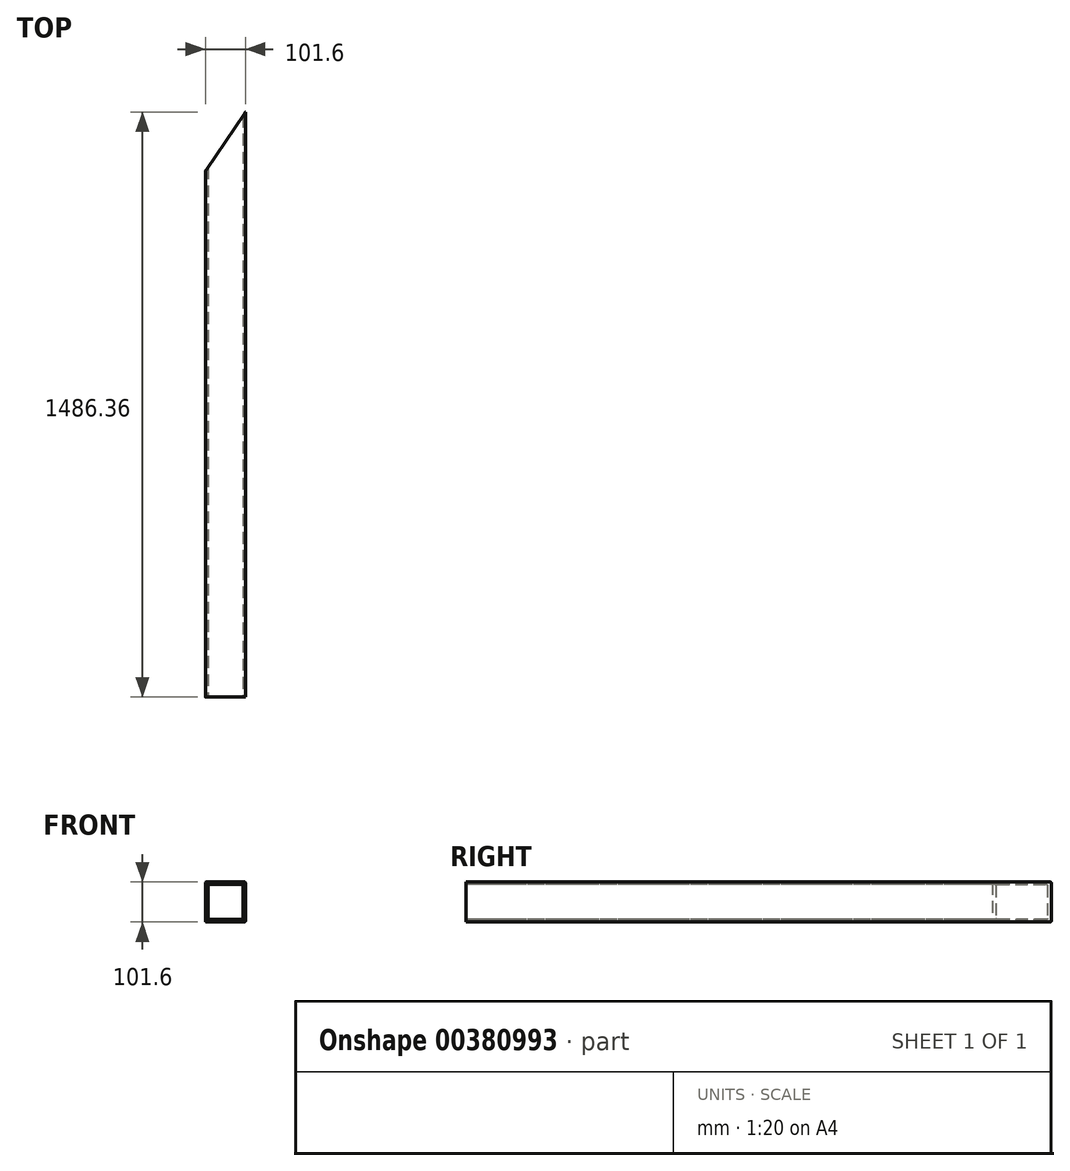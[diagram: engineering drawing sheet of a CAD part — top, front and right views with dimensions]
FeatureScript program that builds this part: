
annotation { "Feature Type Name" : "Feature", "Feature Type Description" : "" }
export const myFeature = defineFeature(function(context is Context, id is Id, definition is map)
    precondition{}
    {
        {
            var Q0;
            Q0=qCreatedBy(makeId("Top.planeOp"),FACE);
            var sketch = newSketch(context, id + "F0", { "sketchPlane" : qUnion([Q0])});
            skLineSegment(sketch, "E0.left", {"start": v(560, 75) * mm, "end": v(560, -75) * mm});
            skPoint(sketch, "E0.middle", {"position": v(0, 0) * mm});
            skLineSegment(sketch, "E1.top", {"start": v(560, -1035) * mm, "end": v(458.4, -1035) * mm});
            skLineSegment(sketch, "E1.left", {"start": v(560, 75) * mm, "end": v(560, -1035) * mm});
            skLineSegment(sketch, "E1.right", {"start": v(458.4, -75) * mm, "end": v(458.4, -1035) * mm});
            skLineSegment(sketch, "E2", {"start": v(458.4, -75) * mm, "end": v(560, 75) * mm});
            skLineSegment(sketch, "E3.left", {"start": v(560, 451.36) * mm, "end": v(560, 301.36) * mm});
            skPoint(sketch, "E3.middle", {"position": v(0, 376.36) * mm});
            skLineSegment(sketch, "E4.top", {"start": v(560, -658.64) * mm, "end": v(458.4, -658.64) * mm});
            skLineSegment(sketch, "E4.left", {"start": v(560, 451.36) * mm, "end": v(560, -658.64) * mm});
            skLineSegment(sketch, "E4.right", {"start": v(458.4, 301.36) * mm, "end": v(458.4, -658.64) * mm});
            skLineSegment(sketch, "E5", {"start": v(458.4, 301.36) * mm, "end": v(560, 451.36) * mm});
            skSolve(sketch);
        }
        {
            var Q0;
            Q0=qSketchRegion(id+"F0",true);
            extrude(context, id + "F1", {"entities" : qUnion([Q0]), "endBound" : BoundingType.SYMMETRIC, "depth" : 101.6 * mm});
        }
        {
            var Q0;
            Q0=makeQuery(id+"F1.opExtrude","SWEPT_FACE",FACE,{"disambiguationData":[OSD([sQuery(id+"F0.wireOp",EDGE,"E1.top")])]});
            var sketch = newSketch(context, id + "F2", { "sketchPlane" : qUnion([Q0])});
            skLineSegment(sketch, "E6.MirrorCS", {"start": v(464.75, -44.45) * mm, "end": v(553.65, -44.45) * mm});
            skLineSegment(sketch, "E7.MirrorCS", {"start": v(464.75, 44.45) * mm, "end": v(464.75, -44.45) * mm});
            skLineSegment(sketch, "E8.MirrorCS", {"start": v(464.75, 44.45) * mm, "end": v(553.65, 44.45) * mm});
            skLineSegment(sketch, "E9.MirrorCS", {"start": v(553.65, 44.45) * mm, "end": v(553.65, -44.45) * mm});
            skSolve(sketch);
        }
        {
            var Q0;
            Q0=makeQuery(id+"F2.imprint","IMPRINT",FACE,{"disambiguationData":[TD([[makeQuery(id+"F2.imprint","IMPRINT",EDGE,{"derivedFrom":sQuery(id+"F2.wireOp",EDGE,"E8.MirrorCS")}),-1.0]])]});
            extrude(context, id + "F3", {"entities" : qUnion([Q0]), "operationType" : NewBodyOperationType.REMOVE, "endBound" : BoundingType.UP_TO_NEXT, "oppositeDirection" : true, "depth" : 25 * mm});
        }
        {
            var Q0;
            Q0=makeQuery(id+"F1.opExtrude","CAP_EDGE",EDGE,{"disambiguationData":[OSD([sQuery(id+"F0.wireOp",EDGE,"E1.left"),sQuery(id+"F0.wireOp",EDGE,"E4.left")])],"isStart":false});
            var Q1;
            Q1=makeQuery(id+"F1.opExtrude","CAP_EDGE",EDGE,{"disambiguationData":[OSD([sQuery(id+"F0.wireOp",EDGE,"E1.right"),sQuery(id+"F0.wireOp",EDGE,"E4.right")])],"isStart":false});
            var Q2;
            Q2=makeQuery(id+"F1.opExtrude","CAP_EDGE",EDGE,{"disambiguationData":[OSD([sQuery(id+"F0.wireOp",EDGE,"E1.right"),sQuery(id+"F0.wireOp",EDGE,"E4.right")])],"isStart":true});
            var Q3;
            Q3=makeQuery(id+"F1.opExtrude","CAP_EDGE",EDGE,{"disambiguationData":[OSD([sQuery(id+"F0.wireOp",EDGE,"E1.left"),sQuery(id+"F0.wireOp",EDGE,"E4.left")])],"isStart":true});
            var Q4;
            Q4=makeQuery(id+"F3.boolean.opBoolean","COPY",EDGE,{"derivedFrom":makeQuery(id+"F3.opExtrude","SWEPT_EDGE",EDGE,{"disambiguationData":[OSD([sQuery(id+"F2.wireOp",EDGE,"E8.MirrorCS"),sQuery(id+"F2.wireOp",EDGE,"E7.MirrorCS")])]})});
            var Q5;
            Q5=makeQuery(id+"F3.boolean.opBoolean","COPY",EDGE,{"derivedFrom":makeQuery(id+"F3.opExtrude","SWEPT_EDGE",EDGE,{"disambiguationData":[OSD([sQuery(id+"F2.wireOp",EDGE,"E8.MirrorCS"),sQuery(id+"F2.wireOp",EDGE,"E9.MirrorCS")])]})});
            var Q6;
            Q6=makeQuery(id+"F3.boolean.opBoolean","COPY",EDGE,{"derivedFrom":makeQuery(id+"F3.opExtrude","SWEPT_EDGE",EDGE,{"disambiguationData":[OSD([sQuery(id+"F2.wireOp",EDGE,"E9.MirrorCS"),sQuery(id+"F2.wireOp",EDGE,"E6.MirrorCS")])]})});
            var Q7;
            Q7=makeQuery(id+"F3.boolean.opBoolean","COPY",EDGE,{"derivedFrom":makeQuery(id+"F3.opExtrude","SWEPT_EDGE",EDGE,{"disambiguationData":[OSD([sQuery(id+"F2.wireOp",EDGE,"E6.MirrorCS"),sQuery(id+"F2.wireOp",EDGE,"E7.MirrorCS")])]})});
            fillet(context, id + "F4", {"entities" : qUnion([Q0, Q1, Q2, Q3, Q4, Q5, Q6, Q7]), "radius" : 2.5 * mm, "tangentPropagation" : true, "allowEdgeOverflow" : false});
        }
    });
